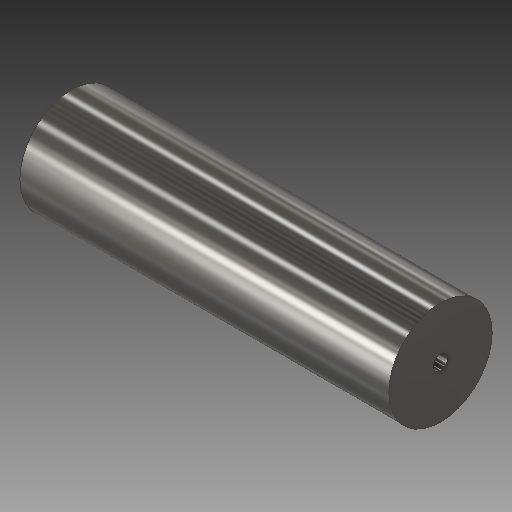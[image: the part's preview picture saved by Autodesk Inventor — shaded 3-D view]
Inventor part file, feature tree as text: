
AUTODESK INVENTOR PART (.ipt)
format: ipt  version: 2018 (Build 220112000, 112)  size: 176,640 bytes
history: native  units: in
note: dims shown in document units (in); Inventor stores cm internally (conversion verified against a paired STEP export)
features: reference x3, other x3, revolve x1, sketch x1
ambient origin geometry x8: Origin, YZ Plane, XZ Plane, XY Plane, X Axis, Y Axis, Z Axis, Center Point
bodies: Solid1 (feature_tree)
feature tree (8):
  revolve  "Revolution1"  Angle=90.0deg
  sketch  "Sketch1"  dims[d1=28.0in d4=90.0deg d5=2.0in]
  reference  "Reference1"
  reference  "Reference2"
  reference  "Reference3"
  other  "<userpath>\Documents\Caleb School 2017-2018\GroupProject\BearingAssyCJE.iam"
  other  "BearingAssyCJE.iam"
  other  "BearingHolderCJE:1"
